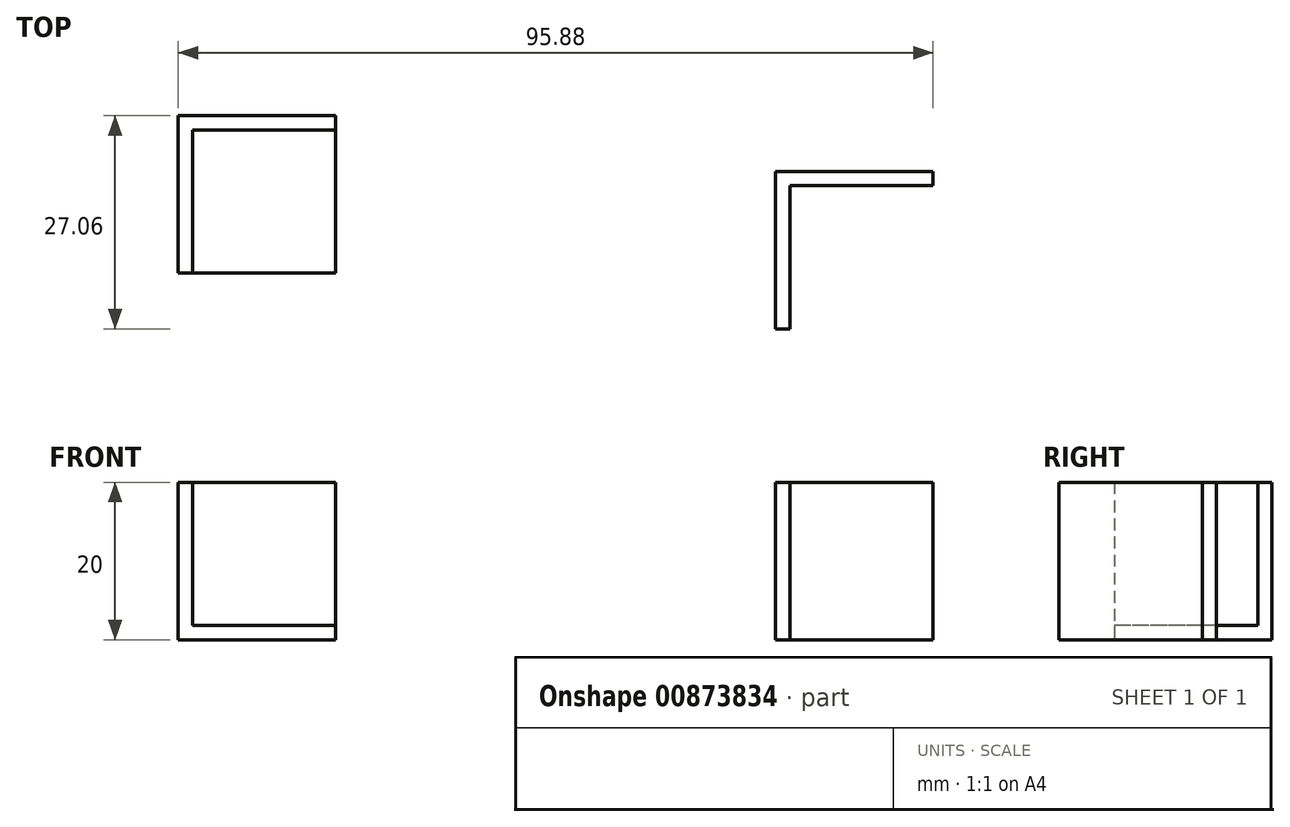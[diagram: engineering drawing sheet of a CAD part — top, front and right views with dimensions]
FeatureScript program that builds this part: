
annotation { "Feature Type Name" : "Feature", "Feature Type Description" : "" }
export const myFeature = defineFeature(function(context is Context, id is Id, definition is map)
    precondition{}
    {
        {
            var Q0;
            Q0=qCreatedBy(makeId("Top.planeOp"),FACE);
            var sketch = newSketch(context, id + "F0", { "sketchPlane" : qUnion([Q0])});
            skLineSegment(sketch, "E0.bottom", {"start": v(-58.02, 51.6) * mm, "end": v(-38.02, 51.6) * mm});
            skLineSegment(sketch, "E0.top", {"start": v(-58.02, 31.6) * mm, "end": v(-38.02, 31.6) * mm});
            skLineSegment(sketch, "E0.left", {"start": v(-58.02, 51.6) * mm, "end": v(-58.02, 31.6) * mm});
            skLineSegment(sketch, "E0.right", {"start": v(-38.02, 51.6) * mm, "end": v(-38.02, 31.6) * mm});
            skLineSegment(sketch, "E1.bottom", {"start": v(17.86, 44.54) * mm, "end": v(19.66, 44.54) * mm});
            skLineSegment(sketch, "E1.top", {"start": v(17.86, 24.54) * mm, "end": v(19.66, 24.54) * mm});
            skLineSegment(sketch, "E1.left", {"start": v(17.86, 44.54) * mm, "end": v(17.86, 24.54) * mm});
            skLineSegment(sketch, "E1.right", {"start": v(19.66, 42.74) * mm, "end": v(19.66, 24.54) * mm});
            skLineSegment(sketch, "E2.bottom", {"start": v(19.66, 44.54) * mm, "end": v(37.86, 44.54) * mm});
            skLineSegment(sketch, "E2.top", {"start": v(19.66, 42.74) * mm, "end": v(37.86, 42.74) * mm});
            skLineSegment(sketch, "E2.right", {"start": v(37.86, 44.54) * mm, "end": v(37.86, 42.74) * mm});
            skLineSegment(sketch, "E3.0", {"start": v(-56.22, 49.8) * mm, "end": v(-56.22, 31.6) * mm});
            skLineSegment(sketch, "E3.1", {"start": v(-56.22, 49.8) * mm, "end": v(-38.02, 49.8) * mm});
            skSolve(sketch);
        }
        {
            var Q0;
            {var subQ3=sQuery(id+"F0.wireOp",EDGE,"E3.0");Q0=makeQuery(id+"F0.imprint","IMPRINT",FACE,{"disambiguationData":[TD([[makeQuery(id+"F0.imprint","IMPRINT",EDGE,{"derivedFrom":subQ3}),1.0]])]});}
            extrude(context, id + "F1", {"entities" : qUnion([Q0]), "depth" : 1.8 * mm, "offsetDistance" : 25 * mm});
        }
        {
            var Q0;
            {var subQ1=sQuery(id+"F0.wireOp",EDGE,"E0.bottom");Q0=makeQuery(id+"F0.imprint","IMPRINT",FACE,{"disambiguationData":[TD([[makeQuery(id+"F0.imprint","IMPRINT",EDGE,{"derivedFrom":subQ1}),-1.0]])]});}
            extrude(context, id + "F2", {"entities" : qUnion([Q0]), "operationType" : NewBodyOperationType.ADD, "depth" : 20 * mm, "offsetDistance" : 25 * mm});
        }
        {
            var Q0;
            Q0=makeQuery(id+"F0.imprint","IMPRINT",FACE,{"disambiguationData":[TD([[makeQuery(id+"F0.imprint","IMPRINT",EDGE,{"derivedFrom":sQuery(id+"F0.wireOp",EDGE,"E1.bottom")}),-1.0]])]});
            extrude(context, id + "F3", {"entities" : qUnion([Q0]), "depth" : 20 * mm, "offsetDistance" : 25 * mm});
        }
    });
